# Revit family: Double_Towel_Bar-Grohe-Essentials-40802_Series
name_source: partatom
category: Specialty Equipment
revit_build: Autodesk Revit 2018 (Build: 20170223_1515(x64)
units: mm (PartAtom-declared; Revit-internal decimal feet)

## family parameters
Cut with Voids When Loaded = No
Host = Face
OmniClass Number = 23.40.20.21.27
OmniClass Title = Towel Bars
Part Type = Normal
Room Calculation Point = No
Round Connector Dimension = Use Diameter
Shared = Yes

## types (2) — shared parameters
Assembly Code = D2010710
Description = ESSENTIALS 654mm Double Towel Bar
Height = 5 cm
Installation Type = Wall Mounted
Length = 60 cm
Manufacturer = Grohe
Price = Prices may vary. Please consult Manufacturer Representative for most up-to-date price list.
Product Documentation Link = https://americanstandard.box.com
Product Page URL = https://www.grohe.us
Region = North America
URL = https://www.grohe.us
Warranty Information = Limited Lifetime Warranty
Width = 11 cm
zero-valued in all types: Default Elevation

## per-type parameters (varying)
| type | Body Material | Material |
| 40802001 | Metal-Grohe-001-Starlight_Chrome | Metal-Grohe-001-Starlight_Chrome |
| 40802EN1 | Metal-Grohe-EN1-Brushed_Nickel | Metal-Grohe-EN1-Brushed_Nickel |

note: column(s) folded — value = type name in every type: Model

## geometry (parser evidence)
native form markers: Sweep x3
no freeform markers — native parametric forms only
